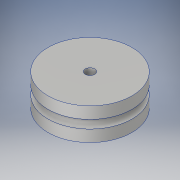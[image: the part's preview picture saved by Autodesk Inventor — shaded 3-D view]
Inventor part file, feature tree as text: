
AUTODESK INVENTOR PART (.ipt)
format: ipt  version: 2018 (Build 220112000, 112)  size: 134,656 bytes
history: native  units: in
note: dims shown in document units (in); Inventor stores cm internally (conversion verified against a paired STEP export)
features: sketch x2, revolve x1, extrude x1
ambient origin geometry x8: Origin, YZ Plane, XZ Plane, XY Plane, X Axis, Y Axis, Z Axis, Center Point
bodies: Solid1 (feature_tree)
feature tree (4):
  revolve  "Revolution1"  [1 undecoded]
  extrude  "Extrusion1"  TaperAngle=90.0deg  [1 undecoded]
  sketch  "Sketch1"  dims[d0=1.1in d1=0.834in]
  sketch  "Sketch2"  dims[d2=0.22in d3=90.0deg d4=0.25in d5=1.0in d6=0.0in]
note: 2 required parameter values undecoded (feature->parameter linkage not recoverable at this tier; creation-order binding heuristic only, values carry confidence <= 0.55)